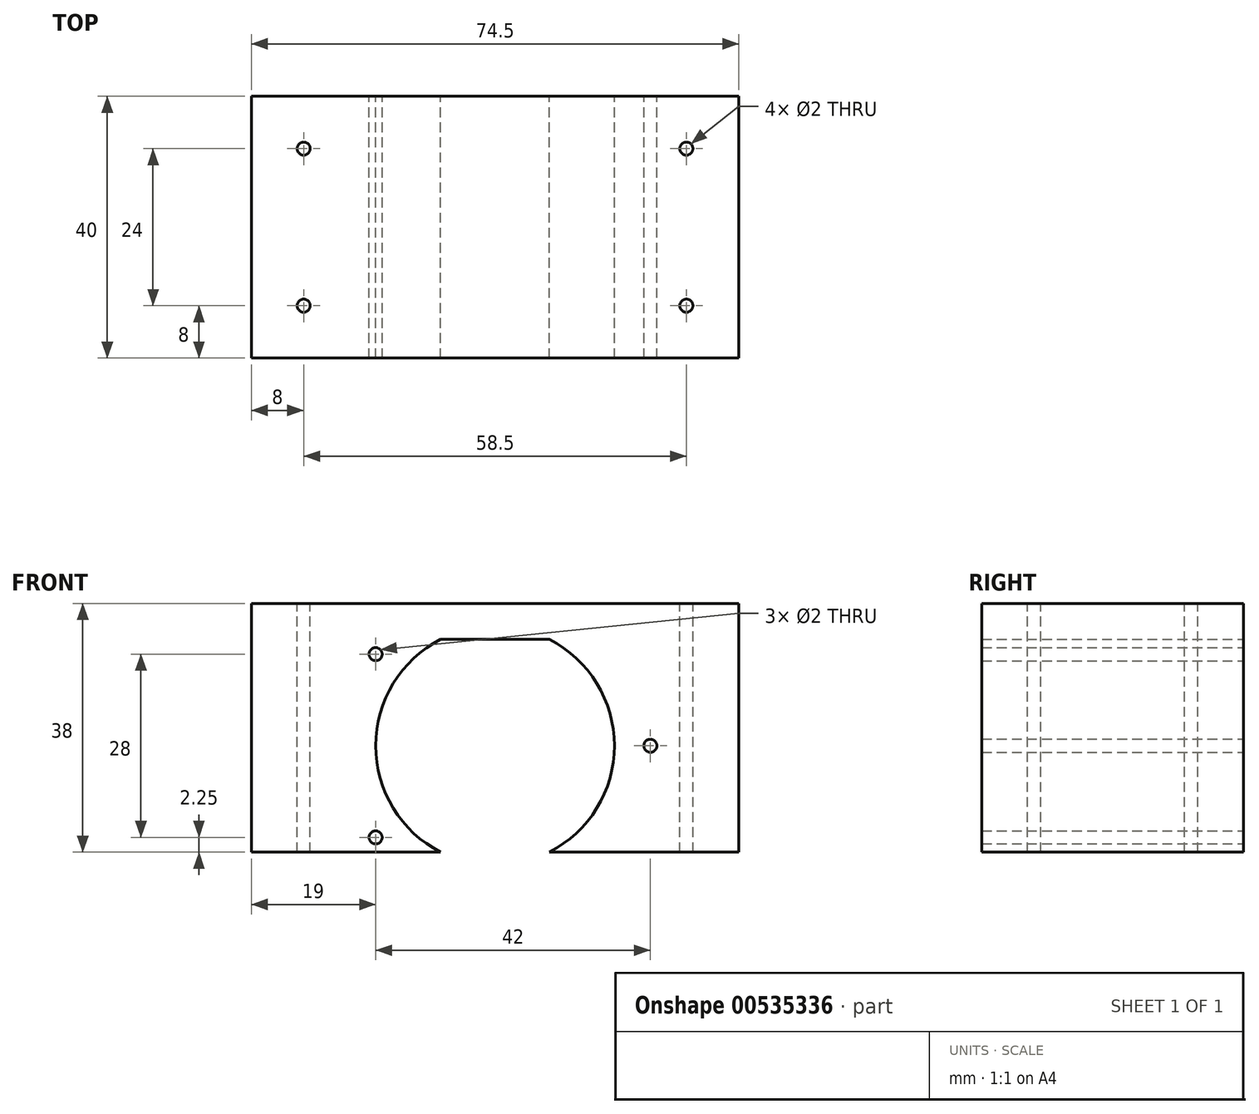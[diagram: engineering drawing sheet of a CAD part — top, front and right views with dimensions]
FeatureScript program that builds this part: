
annotation { "Feature Type Name" : "Feature", "Feature Type Description" : "" }
export const myFeature = defineFeature(function(context is Context, id is Id, definition is map)
    precondition{}
    {
        {
            var Q0;
            Q0=qCreatedBy(makeId("Front.planeOp"),FACE);
            var sketch = newSketch(context, id + "F0", { "sketchPlane" : qUnion([Q0])});
            skLineSegment(sketch, "E0.bottom", {"start": v(-37.25, 21.75) * mm, "end": v(37.25, 21.75) * mm});
            skLineSegment(sketch, "E0.top", {"start": v(-37.25, -16.25) * mm, "end": v(37.25, -16.25) * mm});
            skLineSegment(sketch, "E0.left", {"start": v(-37.25, 21.75) * mm, "end": v(-37.25, -16.25) * mm});
            skLineSegment(sketch, "E0.right", {"start": v(37.25, 21.75) * mm, "end": v(37.25, -16.25) * mm});
            skLineSegment(sketch, "E1", {"start": v(-37.25, 0) * mm, "end": v(37.25, 0) * mm, "construction": true});
            skLineSegment(sketch, "E2", {"start": v(0, 21.75) * mm, "end": v(0, -16.25) * mm, "construction": true});
            skCircle(sketch, "E3", {"center": v(0, 0) * mm, "radius": 18.25 * mm});
            skLineSegment(sketch, "E4", {"start": v(37.25, 16.25) * mm, "end": v(-37.25, 16.25) * mm});
            skCircle(sketch, "E5", {"center": v(23.75, 0) * mm, "radius": 1 * mm});
            skPoint(sketch, "E6", {"position": v(-18.25, 0) * mm});
            skLineSegment(sketch, "E7", {"start": v(-18.25, 21.75) * mm, "end": v(-18.25, -16.25) * mm, "construction": true});
            skCircle(sketch, "E8", {"center": v(-18.25, 14) * mm, "radius": 1 * mm});
            skCircle(sketch, "E9", {"center": v(-18.25, -14) * mm, "radius": 1 * mm});
            skSolve(sketch);
        }
        {
            var Q0;
            Q0=makeQuery(id+"F0.imprint","IMPRINT",FACE,{"disambiguationData":[TD([[makeQuery(id+"F0.imprint","IMPRINT",EDGE,{"derivedFrom":sQuery(id+"F0.wireOp",EDGE,"E8")}),-1.0]])]});
            var Q1;
            {var subQ5=sQuery(id+"F0.wireOp",EDGE,"E0.bottom");Q1=makeQuery(id+"F0.imprint","IMPRINT",FACE,{"disambiguationData":[TD([[makeQuery(id+"F0.imprint","IMPRINT",EDGE,{"derivedFrom":subQ5}),-1.0]])]});}
            var Q2;
            Q2=makeQuery(id+"F0.imprint","IMPRINT",FACE,{"disambiguationData":[TD([[makeQuery(id+"F0.imprint","IMPRINT",EDGE,{"derivedFrom":sQuery(id+"F0.wireOp",EDGE,"E5")}),-1.0]])]});
            var Q3;
            {var subQ0=sQuery(id+"F0.wireOp",EDGE,"E4");var subQ1=sQuery(id+"F0.wireOp",EDGE,"E3");var subQ2=makeQuery(id+"F0.imprint","INTERSECT",VERTEX,{"disambiguationData":[OD(0.0)],"derivedFrom":[subQ1,subQ0]});Q3=makeQuery(id+"F0.imprint","IMPRINT",FACE,{"disambiguationData":[TD([[makeQuery(id+"F0.imprint","IMPRINT",EDGE,{"disambiguationData":[TD([[subQ2,1.0]])],"derivedFrom":subQ1}),1.0]])]});}
            extrude(context, id + "F1", {"entities" : qUnion([Q0, Q1, Q2, Q3]), "depth" : 40 * mm, "offsetDistance" : 25 * mm});
        }
        {
            var Q0;
            Q0=makeQuery(id+"F1.opExtrude","SWEPT_FACE",FACE,{"disambiguationData":[OSD([sQuery(id+"F0.wireOp",EDGE,"E0.bottom")])]});
            var sketch = newSketch(context, id + "F2", { "sketchPlane" : qUnion([Q0])});
            skLineSegment(sketch, "E10", {"start": v(-29.25, 0) * mm, "end": v(-29.25, -40) * mm, "construction": true});
            skCircle(sketch, "E11", {"center": v(-29.25, -8) * mm, "radius": 1 * mm});
            skCircle(sketch, "E12", {"center": v(-29.25, -32) * mm, "radius": 1 * mm});
            skLineSegment(sketch, "E13", {"start": v(0, 0) * mm, "end": v(0, -40) * mm, "construction": true});
            skCircle(sketch, "E14.MirrorC", {"center": v(29.25, -32) * mm, "radius": 1 * mm});
            skCircle(sketch, "E15.MirrorC", {"center": v(29.25, -8) * mm, "radius": 1 * mm});
            skSolve(sketch);
        }
        {
            var Q0;
            Q0 = qSketchRegion(id + "F2", true);
            extrude(context, id + "F3", {"entities" : qUnion([Q0]), "operationType" : NewBodyOperationType.REMOVE, "oppositeDirection" : true, "depth" : 46.1 * mm, "offsetDistance" : 25 * mm});
        }
    });
